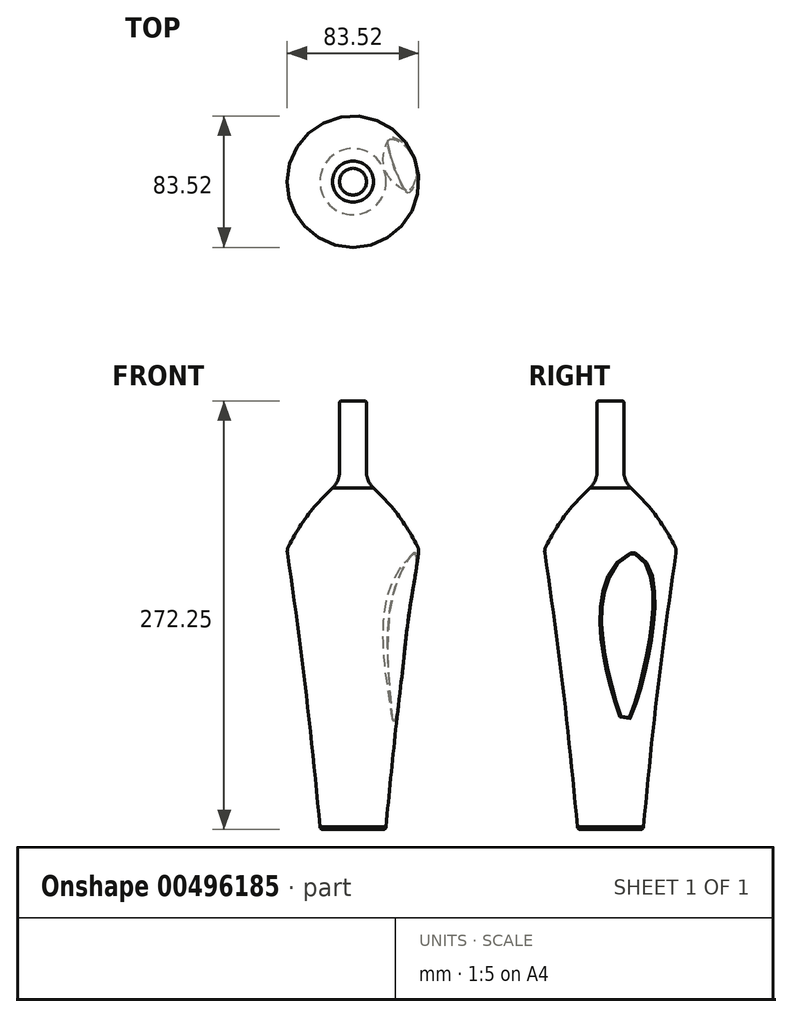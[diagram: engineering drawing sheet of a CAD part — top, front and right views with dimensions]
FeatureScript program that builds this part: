
annotation { "Feature Type Name" : "Feature", "Feature Type Description" : "" }
export const myFeature = defineFeature(function(context is Context, id is Id, definition is map)
    precondition{}
    {
        {
            var Q0;
            Q0=qCreatedBy(makeId("Front.planeOp"),FACE);
            var sketch = newSketch(context, id + "F0", { "sketchPlane" : qUnion([Q0])});
            skLineSegment(sketch, "E0", {"start": v(0, 0) * mm, "end": v(0, 272.25) * mm});
            skLineSegment(sketch, "E1", {"start": v(-8.5, 271.25) * mm, "end": v(-8.5, 227.6) * mm});
            skLineSegment(sketch, "E2", {"start": v(-7.5, 272.25) * mm, "end": v(0, 272.25) * mm});
            skPoint(sketch, "E3.visualSharp", {"position": v(-8.5, 214.34) * mm});
            skPoint(sketch, "E4.visualSharp", {"position": v(-8.5, 272.25) * mm});
            skArc(sketch, "E4.filletArc", {"start": v(-7.5, 272.25) * mm, "mid": v(-8.2, 271.96) * mm, "end": v(-8.5, 271.25) * mm});
            skLineSegment(sketch, "E5", {"start": v(0, 0) * mm, "end": v(0, -25) * mm});
            skLineSegment(sketch, "E6", {"start": v(-42, 177.76) * mm, "end": v(-21.01, 1.76) * mm, "construction": true});
            skPoint(sketch, "E7.visualSharp", {"position": v(-43.17, 187.58) * mm});
            skLineSegment(sketch, "E8", {"start": v(0, 0) * mm, "end": v(-19.03, 0) * mm});
            skPoint(sketch, "E9.visualSharp", {"position": v(-20.8, 0) * mm});
            skArc(sketch, "E9.filletArc", {"start": v(-21.01, 1.76) * mm, "mid": v(-20.36, 0.5) * mm, "end": v(-19.03, 0) * mm});
            skPoint(sketch, "E10.visualSharp", {"position": v(-8.5, 221.25) * mm});
            skArc(sketch, "E10.filletArc", {"start": v(-13.05, 216.84) * mm, "mid": v(-9.68, 221.76) * mm, "end": v(-8.5, 227.6) * mm});
            skArc(sketch, "E11", {"start": v(-21.01, 1.76) * mm, "mid": v(-30.05, 88.84) * mm, "end": v(-41.68, 175.61) * mm});
            skArc(sketch, "E12", {"start": v(-13.05, 216.84) * mm, "mid": v(-28.74, 199.6) * mm, "end": v(-41.02, 179.77) * mm});
            skPoint(sketch, "E13.visualSharp", {"position": v(-42, 177.76) * mm});
            skArc(sketch, "E13.filletArc", {"start": v(-41.02, 179.77) * mm, "mid": v(-41.67, 177.74) * mm, "end": v(-41.68, 175.61) * mm});
            skSolve(sketch);
        }
        {
            var Q0;
            {var subQ0=sQuery(id+"F0.wireOp",EDGE,"E0");Q0=makeQuery(id+"F0.imprint","IMPRINT",FACE,{"disambiguationData":[TD([[makeQuery(id+"F0.imprint","IMPRINT",EDGE,{"derivedFrom":subQ0}),1.0]])]});}
            var Q1;
            Q1=sQuery(id+"F0.wireOp",EDGE,"E0");
            revolve(context, id + "F1", {"entities" : qUnion([Q0]), "axis" : qUnion([Q1]), "revolveType" : RevolveType.FULL});
        }
        {
            var Q0;
            Q0=qCreatedBy(makeId("Right.planeOp"),FACE);
            var sketch = newSketch(context, id + "F2", { "sketchPlane" : qUnion([Q0])});
            skLineSegment(sketch, "E14", {"start": v(0, 0) * mm, "end": v(0, -65.32) * mm});
            skSolve(sketch);
        }
        {
            var Q0;
            Q0=sQuery(id+"F2.wireOp",EDGE,"E14");
            cPlane(context, id + "F3", {"entities" : qUnion([Q0]), "cplaneType" : CPlaneType.LINE_ANGLE, "offset" : 25 * mm, "angle" : 70 * degree, "width" : 150 * mm, "height" : 150 * mm});
        }
        {
            var Q0;
            Q0=qCreatedBy(id+"F3.planeOp",FACE);
            var sketch = newSketch(context, id + "F4", { "sketchPlane" : qUnion([Q0])});
            skLineSegment(sketch, "E15", {"start": v(-53.7, 183.3) * mm, "end": v(-29.69, 53.25) * mm});
            skFitSpline(sketch, "E16", {"points": [v(-53.7, 183.3) * mm, v(-29.69, 53.25) * mm], "startDerivative": vector(136.24, -68.42) * mm, "endDerivative": vector(-21.8, -155.94) * mm});
            skSolve(sketch);
        }
        {
            var Q0;
            Q0=makeQuery(id+"F4.imprint","IMPRINT",FACE,{"disambiguationData":[TD([[makeQuery(id+"F4.imprint","IMPRINT",EDGE,{"derivedFrom":sQuery(id+"F4.wireOp",EDGE,"PWsksZhq-Kbv2-ibrw-MtZP-wMo4pvSYyuIZ")}),1.0]])]});
            var Q1;
            Q1=makeQuery(id+"F4.imprint","IMPRINT",FACE,{"disambiguationData":[TD([[makeQuery(id+"F4.imprint","IMPRINT",EDGE,{"derivedFrom":sQuery(id+"F4.wireOp",EDGE,"E15")}),1.0]])]});
            var Q2;
            Q2=sQuery(id+"F4.wireOp",EDGE,"PWsksZhq-Kbv2-ibrw-MtZP-wMo4pvSYyuIZ");
            var Q3;
            Q3=sQuery(id+"F4.wireOp",EDGE,"E15");
            revolve(context, id + "F5", {"operationType" : NewBodyOperationType.REMOVE, "entities" : qUnion([Q0, Q1]), "surfaceEntities" : qUnion([Q2]), "axis" : qUnion([Q3]), "revolveType" : RevolveType.FULL, "oppositeDirection" : true});
        }
        {
            var Q0;
            Q0=makeQuery(id+"F222g8hhwuNekE7_1.1.F5.boolean.opBoolean","INTERSECT",EDGE,{"derivedFrom":[makeQuery(id+"F1.opRevolve","SWEPT_FACE",FACE,{"disambiguationData":[OSD([sQuery(id+"F0.wireOp",EDGE,"E11")])]}),makeQuery(id+"F222g8hhwuNekE7_1.1.F5.opRevolve","SWEPT_FACE",FACE,{"disambiguationData":[OSD([sQuery(id+"F4.wireOp",EDGE,"E16")])]})]});
            var Q1;
            Q1=makeQuery(id+"F5.boolean.opBoolean","INTERSECT",EDGE,{"derivedFrom":[makeQuery(id+"F1.opRevolve","SWEPT_FACE",FACE,{"disambiguationData":[OSD([sQuery(id+"F0.wireOp",EDGE,"E11")])]}),makeQuery(id+"F5.opRevolve","SWEPT_FACE",FACE,{"disambiguationData":[OSD([sQuery(id+"F4.wireOp",EDGE,"E16")])]})]});
            fillet(context, id + "F6", {"entities" : qUnion([Q0, Q1]), "radius" : 1 * mm, "tangentPropagation" : true, "allowEdgeOverflow" : false});
        }
    });
